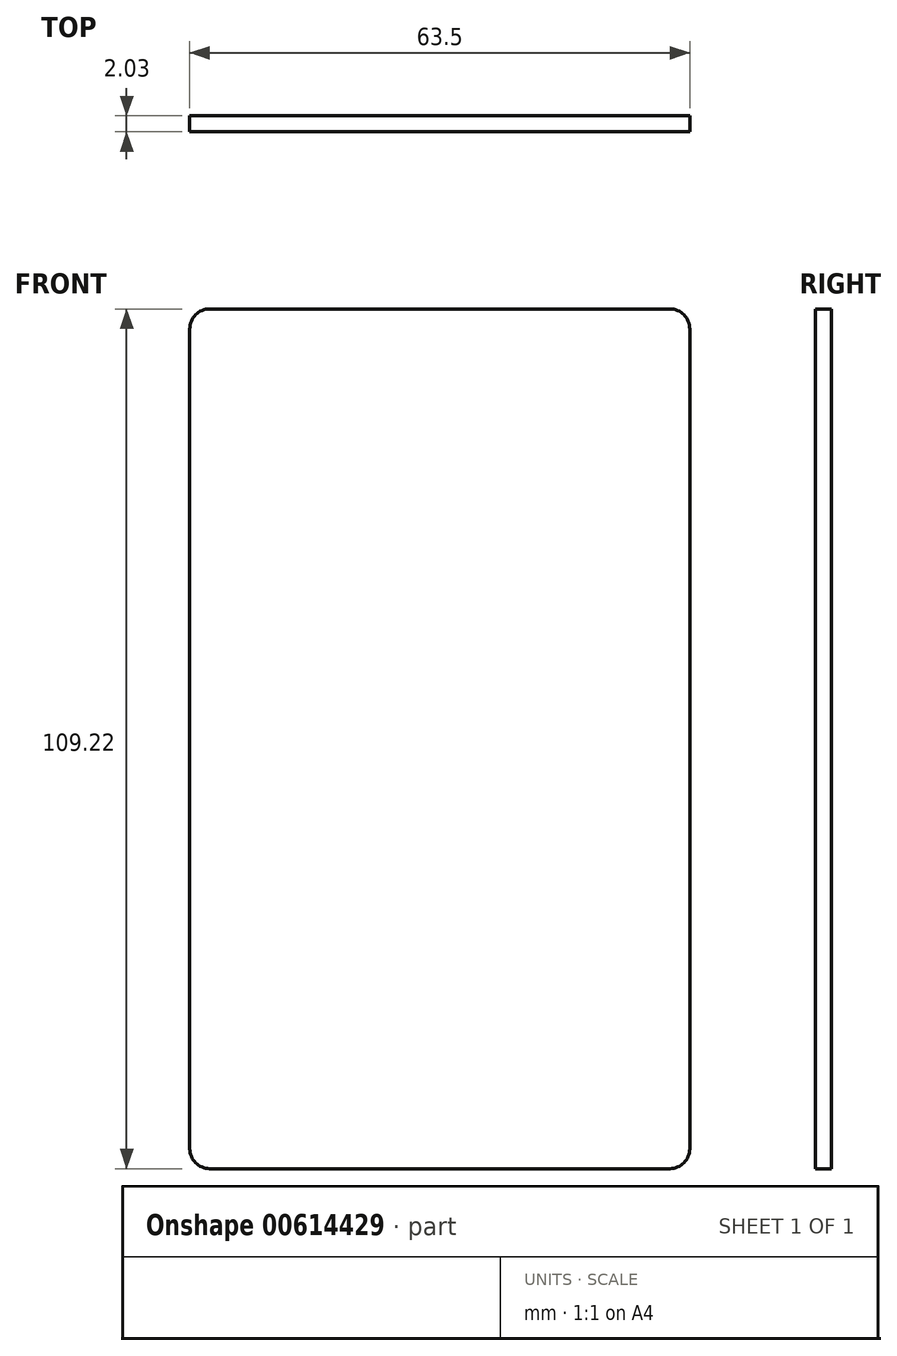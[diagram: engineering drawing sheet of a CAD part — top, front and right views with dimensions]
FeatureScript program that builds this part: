
annotation { "Feature Type Name" : "Feature", "Feature Type Description" : "" }
export const myFeature = defineFeature(function(context is Context, id is Id, definition is map)
    precondition{}
    {
        {
            var Q0;
            Q0=qCreatedBy(makeId("Front.planeOp"),FACE);
            var sketch = newSketch(context, id + "F0", { "sketchPlane" : qUnion([Q0])});
            skLineSegment(sketch, "E0.bottom", {"start": v(-29.2, -54.61) * mm, "end": v(29.21, -54.61) * mm});
            skLineSegment(sketch, "E0.top", {"start": v(-29.2, 54.61) * mm, "end": v(29.2, 54.61) * mm});
            skLineSegment(sketch, "E0.left", {"start": v(-31.75, -52.07) * mm, "end": v(-31.75, 52.07) * mm});
            skLineSegment(sketch, "E0.right", {"start": v(31.75, -52.07) * mm, "end": v(31.75, 52.07) * mm});
            skPoint(sketch, "E0.middle", {"position": v(0, 0) * mm});
            skPoint(sketch, "E1.visualSharp", {"position": v(-31.75, 54.6) * mm});
            skArc(sketch, "E1.filletArc", {"start": v(-29.21, 54.61) * mm, "mid": v(-31, 53.87) * mm, "end": v(-31.75, 52.07) * mm});
            skPoint(sketch, "E2.visualSharp", {"position": v(31.75, 54.61) * mm});
            skArc(sketch, "E2.filletArc", {"start": v(31.75, 52.07) * mm, "mid": v(31, 53.87) * mm, "end": v(29.2, 54.61) * mm});
            skPoint(sketch, "E3.visualSharp", {"position": v(31.75, -54.61) * mm});
            skArc(sketch, "E3.filletArc", {"start": v(29.21, -54.61) * mm, "mid": v(31, -53.87) * mm, "end": v(31.75, -52.07) * mm});
            skPoint(sketch, "E4.visualSharp", {"position": v(-31.75, -54.61) * mm});
            skArc(sketch, "E4.filletArc", {"start": v(-31.75, -52.07) * mm, "mid": v(-31, -53.87) * mm, "end": v(-29.2, -54.61) * mm});
            skSolve(sketch);
        }
        {
            var Q0;
            Q0=qSketchRegion(id+"F0",true);
            extrude(context, id + "F1", {"entities" : qUnion([Q0]), "depth" : 2.03 * mm, "offsetDistance" : 25.4 * mm});
        }
    });
